FCSTD DOCUMENT  (FreeCAD 0.19R24276 (Git))
Label: assembly_1
License: All rights reserved
LicenseURL: http://en.wikipedia.org/wiki/All_rights_reserved
objects: Part::FeaturePython×82, App::LinkGroup×14, App::FeaturePython×4
note: 82 computed .brp shape members not serialized (recipe doc carries the construction recipe); baked Part::Feature solids carry a one-line shape summary decoded from their .brp

FEATURE [Part::FeaturePython] b_motor_mount_001_  label="motor mount_001"  # a2plus imported part (geometry in sourceFile) (typed FeaturePython)
  Placement = pos=(149.38,107.654,7.41064) rot=(-0.700909,0.71325,0;3.14159rad)
  a2p_Version = V0.1
  fixedPosition = false
  objectType = a2pPart
  sourceFile = ./../standard_parts/motor mount.FCStd
  subassemblyImport = false
  timeLastImport = 1.63751e+09
  updateColors = true
FEATURE [Part::FeaturePython] b_motor_mount_001_001  label="motor mount_002"  # a2plus imported part (geometry in sourceFile) (typed FeaturePython)
  Placement = pos=(-148.997,67.9961,7.41064) rot=(0.707107,0.707107,0;3.14159rad)
  a2p_Version = V0.1
  fixedPosition = false
  objectType = a2pPart
  sourceFile = ./../standard_parts/motor mount.FCStd
  subassemblyImport = false
  timeLastImport = 1.63751e+09
  updateColors = true
FEATURE [Part::FeaturePython] b_wheel1_001_  label="wheel1_001"  # a2plus imported part (geometry in sourceFile) (typed FeaturePython)
  Placement = pos=(-170.202,87.0329,-30.5973) rot=(0,0,1;0rad)
  a2p_Version = V0.1
  fixedPosition = false
  objectType = a2pPart
  sourceFile = ./../ROS_Bot_1/my 3D/ASSEM/wheel.stp
  subassemblyImport = false
  timeLastImport = 1.63742e+09
  updateColors = true
FEATURE [Part::FeaturePython] b_motor1_001_  label="motor1_001"  # a2plus imported part (geometry in sourceFile) (typed FeaturePython)
  Placement = pos=(133.059,87.9604,-23.6086) rot=(0.999922,-0.008726,-0.00888;1.55342rad)
  a2p_Version = V0.1
  fixedPosition = false
  objectType = a2pPart
  sourceFile = ./../ROS_Bot_1/my 3D/ASSEM/motor.stp
  subassemblyImport = false
  timeLastImport = 1.6374e+09
  updateColors = true
FEATURE [App::FeaturePython] axisCoincident_003  label="axisCoincident_003__motor1_001"  # a2plus constraint (typed FeaturePython)
  Object1 = b_motor_mount_001_
  Object2 = b_motor1_001_
  ParentTreeObject = -> b_motor_mount_001_
  SubElement1 = Face28
  SubElement2 = Face12
  Suppressed = false
  Type = axial
  directionConstraint = 1
  lockRotation = false
FEATURE [App::FeaturePython] axisCoincident_003_mirror  label="axisCoincident_003__motor mount_001"  # a2plus constraint (typed FeaturePython)
  Object1 = b_motor_mount_001_
  Object2 = b_motor1_001_
  ParentTreeObject = -> b_motor1_001_
  SubElement1 = Face28
  SubElement2 = Face12
  Suppressed = false
  Type = axial
  directionConstraint = 1
  lockRotation = false
FEATURE [App::FeaturePython] axisCoincident_004  label="axisCoincident_004__motor mount_001"  # a2plus constraint (typed FeaturePython)
  Object1 = b_motor1_001_
  Object2 = b_motor_mount_001_
  ParentTreeObject = -> b_motor1_001_
  SubElement1 = Face12
  SubElement2 = Face28
  Suppressed = false
  Type = axial
  directionConstraint = 0
  lockRotation = true
FEATURE [App::FeaturePython] axisCoincident_004_mirror  label="axisCoincident_004__motor1_001"  # a2plus constraint (typed FeaturePython)
  Object1 = b_motor1_001_
  Object2 = b_motor_mount_001_
  ParentTreeObject = -> b_motor_mount_001_
  SubElement1 = Face12
  SubElement2 = Face28
  Suppressed = false
  Type = axial
  directionConstraint = 0
  lockRotation = true
FEATURE [Part::FeaturePython] b_motor1_001_001  label="motor1_002"  # a2plus imported part (geometry in sourceFile) (typed FeaturePython)
  Placement = pos=(-133.004,87.4074,-23.2076) rot=(0.00011,0.700908,0.713251;3.1418rad)
  a2p_Version = V0.1
  fixedPosition = false
  objectType = a2pPart
  sourceFile = ./../ROS_Bot_1/my 3D/ASSEM/motor.stp
  subassemblyImport = false
  timeLastImport = 1.6374e+09
  updateColors = true
FEATURE [Part::FeaturePython] b_wheel1_001_001  label="wheel1_002"  # a2plus imported part (geometry in sourceFile) (typed FeaturePython)
  Placement = pos=(160.198,87.0329,-30.5973) rot=(0,0,1;0rad)
  a2p_Version = V0.1
  fixedPosition = false
  objectType = a2pPart
  sourceFile = ./../ROS_Bot_1/my 3D/ASSEM/wheel.stp
  subassemblyImport = false
  timeLastImport = 1.63742e+09
  updateColors = true
FEATURE [Part::FeaturePython] b_motor_driver_board_001_  label="motor driver board_001"  # a2plus imported part (geometry in sourceFile) (typed FeaturePython)
  Placement = pos=(-45.0132,88.1039,15.6672) rot=(0,0,-1;1.5708rad)
  a2p_Version = V0.1
  fixedPosition = false
  objectType = a2pPart
  sourceFile = ./../standard_parts/motor driver/motor driver board.FCStd
  subassemblyImport = false
  timeLastImport = 1.63729e+09
  updateColors = true
FEATURE [Part::FeaturePython] b_base_1_001_  label="base_1_001"  # a2plus imported part (geometry in sourceFile) (typed FeaturePython)
  a2p_Version = V0.1
  fixedPosition = true
  objectType = a2pPart
  sourceFile = ./base_1.FCStd
  subassemblyImport = false
  timeLastImport = 1.65701e+09
  updateColors = true
FEATURE [Part::FeaturePython] b_top_001_  label="top_001"  # a2plus imported part (geometry in sourceFile) (typed FeaturePython)
  Placement = pos=(-0.376892,0.553345,71.2288) rot=(0,0,1;0rad)
  a2p_Version = V0.1
  fixedPosition = false
  objectType = a2pPart
  sourceFile = ./top.FCStd
  subassemblyImport = false
  timeLastImport = 1.65701e+09
  updateColors = true
FEATURE [Part::FeaturePython] b_lidar1_001_  label="lidar1_001"  # a2plus imported part (geometry in sourceFile) (typed FeaturePython)
  Placement = pos=(36.9558,-4.98086,81.9191) rot=(0.57735,-0.57735,-0.57735;2.0944rad)
  a2p_Version = V0.1
  fixedPosition = false
  objectType = a2pPart
  sourceFile = ./../standard_parts/lidar.stp
  subassemblyImport = false
  timeLastImport = 1.6374e+09
  updateColors = true
FEATURE [Part::FeaturePython] b_guide_wheel1_001_  label="guide_wheel1_001"  # a2plus imported part (geometry in sourceFile) (typed FeaturePython)
  Placement = pos=(-9.92305,-140.014,-21.8192) rot=(0,0,-1;0.017453rad)
  a2p_Version = V0.1
  fixedPosition = false
  objectType = a2pPart
  sourceFile = ./guide_wheel.step
  subassemblyImport = false
  timeLastImport = 1.65702e+09
  updateColors = true
FEATURE [Part::FeaturePython] b_RPi1_001_  label="RPi1_001"  # a2plus imported part (geometry in sourceFile) (typed FeaturePython)
  Placement = pos=(29.8566,29.4806,88.8306) rot=(0.57735,0.57735,0.57735;2.0944rad)
  a2p_Version = V0.1
  fixedPosition = false
  objectType = a2pPart
  sourceFile = ./RPi.step
  subassemblyImport = false
  timeLastImport = 1.65702e+09
  updateColors = true
FEATURE [Part::FeaturePython] b_Atd1_001_  label="Atd1_001"  # a2plus imported part (geometry in sourceFile) (typed FeaturePython)
  Placement = pos=(0.456543,-67.9815,20.7461) rot=(0.707107,-0.707107,0;3.14159rad)
  a2p_Version = V0.1
  fixedPosition = false
  objectType = a2pPart
  sourceFile = ./Atd.step
  subassemblyImport = false
  timeLastImport = 1.65702e+09
  updateColors = true
FEATURE [Part::FeaturePython] b_stand1_001_  label="stand1_001"  # a2plus imported part (geometry in sourceFile) (typed FeaturePython)
  Placement = pos=(-10.3015,-141.085,4.0706) rot=(0,0,1;0rad)
  a2p_Version = V0.1
  fixedPosition = false
  objectType = a2pPart
  sourceFile = ./stand.step
  subassemblyImport = false
  timeLastImport = 1.65702e+09
  updateColors = true
FEATURE [Part::FeaturePython] PcbSpacer  label="M5x8x10-Spacer"  # WARN: FeaturePython — macro-defined, semantics opaque (R4)
  Placement = pos=(24.1,-22.24,10) rot=(0,0,1;0rad)
  baseObject = -> b_base_1_001_ [Edge135]
  diameter = 4
  invert = false
  length = 0
  offset = 0
  width = 0
FEATURE [Part::FeaturePython] PcbSpacer002  label="M5x8x10-Spacer002"  # WARN: FeaturePython — macro-defined, semantics opaque (R4)
  Placement = pos=(-25.12,-29.42,10) rot=(0,0,1;0rad)
  baseObject = -> b_base_1_001_ [Edge125]
  diameter = 4
  invert = false
  length = 0
  offset = 0
  width = 0
FEATURE [Part::FeaturePython] PcbSpacer004  label="M5x8x10-Spacer004"  # WARN: FeaturePython — macro-defined, semantics opaque (R4)
  Placement = pos=(-24.52,-104.82,10) rot=(0,0,1;0rad)
  baseObject = -> b_base_1_001_ [Edge123]
  diameter = 4
  invert = false
  length = 0
  offset = 0
  width = 0
FEATURE [Part::FeaturePython] PcbSpacer006  label="M5x8x10-Spacer006"  # WARN: FeaturePython — macro-defined, semantics opaque (R4)
  Placement = pos=(24.1,-104.82,10) rot=(0,0,1;0rad)
  baseObject = -> b_base_1_001_ [Edge131]
  diameter = 4
  invert = false
  length = 0
  offset = 0
  width = 0
FEATURE [App::LinkGroup] LinkGroup
  ElementList = -> [PcbSpacer,PcbSpacer002,PcbSpacer004,PcbSpacer006]
  LinkMode = 0
  Placement = pos=(0,-3.8147e-06,-3.8147e-06) rot=(0,0,1;0rad)
FEATURE [Part::FeaturePython] PcbSpacer007  label="M4x7x5-Spacer"  # WARN: FeaturePython — macro-defined, semantics opaque (R4)
  Placement = pos=(34.12,85.08,10) rot=(0,0,1;0rad)
  baseObject = -> b_base_1_001_ [Edge173]
  diameter = 3
  invert = false
  length = 0
  offset = 0
  width = 0
FEATURE [Part::FeaturePython] PcbSpacer009  label="M4x7x5-Spacer002"  # WARN: FeaturePython — macro-defined, semantics opaque (R4)
  Placement = pos=(-21.75,85.08,10) rot=(0,0,1;0rad)
  baseObject = -> b_base_1_001_ [Edge157]
  diameter = 3
  invert = false
  length = 0
  offset = 0
  width = 0
FEATURE [Part::FeaturePython] PcbSpacer011  label="M4x7x5-Spacer004"  # WARN: FeaturePython — macro-defined, semantics opaque (R4)
  Placement = pos=(34.12,6.36,10) rot=(0,0,1;0rad)
  baseObject = -> b_base_1_001_ [Edge171]
  diameter = 3
  invert = false
  length = 0
  offset = 0
  width = 0
FEATURE [Part::FeaturePython] PcbSpacer013  label="M4x7x5-Spacer006"  # WARN: FeaturePython — macro-defined, semantics opaque (R4)
  Placement = pos=(-21.75,6.36,10) rot=(0,0,1;0rad)
  baseObject = -> b_base_1_001_ [Edge155]
  diameter = 3
  invert = false
  length = 0
  offset = 0
  width = 0
FEATURE [App::LinkGroup] LinkGroup001
  ElementList = -> [PcbSpacer007,PcbSpacer009,PcbSpacer011,PcbSpacer013]
  LinkMode = 0
  Placement = pos=(0,2.38419e-07,-9.53674e-07) rot=(0,0,1;0rad)
FEATURE [Part::FeaturePython] Screw001  label="M2.5x3-Screw"  # Fasteners workbench fastener (typed FeaturePython)
  Placement = pos=(-25.6369,-11.9567,71.2288) rot=(-1,0,0;3.14159rad)
  baseObject = -> b_top_001_ [Edge32]
  diameter = 3
  invert = true
  length = 0
  lengthCustom = 3
  matchOuter = false
  offset = 0
  thread = false
  type = 35
FEATURE [Part::FeaturePython] Screw003  label="M2.5x3-Screw015"  # Fasteners workbench fastener (typed FeaturePython)
  Placement = pos=(30.3331,-11.9567,71.2288) rot=(-1,0,0;3.14159rad)
  baseObject = -> b_top_001_ [Edge36]
  diameter = 3
  invert = true
  length = 0
  lengthCustom = 3
  matchOuter = false
  offset = 0
  thread = false
  type = 35
FEATURE [Part::FeaturePython] Screw005  label="M2.5x3-Screw016"  # Fasteners workbench fastener (typed FeaturePython)
  Placement = pos=(-18.1469,-81.9067,71.2288) rot=(-1,0,0;3.14159rad)
  baseObject = -> b_top_001_ [Edge28]
  diameter = 3
  invert = true
  length = 0
  lengthCustom = 3
  matchOuter = false
  offset = 0
  thread = false
  type = 35
FEATURE [Part::FeaturePython] Screw007  label="M2.5x3-Screw017"  # Fasteners workbench fastener (typed FeaturePython)
  Placement = pos=(22.8531,-81.9667,71.2288) rot=(-1,0,0;3.14159rad)
  baseObject = -> b_top_001_ [Edge30]
  diameter = 3
  invert = true
  length = 0
  lengthCustom = 3
  matchOuter = false
  offset = 0
  thread = false
  type = 35
FEATURE [App::LinkGroup] LinkGroup002
  ElementList = -> [Screw001,Screw003,Screw005,Screw007]
  LinkMode = 0
FEATURE [Part::FeaturePython] Screw  label="M4x5-Screw"  # Fasteners workbench fastener (typed FeaturePython)
  Placement = pos=(-148.997,103.616,-23.3051) rot=(0,-1,0;1.5708rad)
  baseObject = -> b_motor_mount_001_001 [Edge55]
  diameter = 6
  invert = true
  length = 0
  lengthCustom = 5
  matchOuter = false
  offset = 0
  thread = false
  type = 35
FEATURE [Part::FeaturePython] Screw009  label="M4x5-Screw001"  # Fasteners workbench fastener (typed FeaturePython)
  Placement = pos=(-150.497,72.6161,-23.3051) rot=(0,-1,0;1.5708rad)
  baseObject = -> b_motor_mount_001_001 [Edge47]
  diameter = 3
  invert = true
  length = 0
  lengthCustom = 5
  matchOuter = false
  offset = 0
  thread = false
  type = 15
FEATURE [App::LinkGroup] LinkGroup003
  ElementList = -> [Screw,Screw009]
  LinkMode = 0
FEATURE [Part::FeaturePython] Screw010  label="(M3.5)x5-Screw"  # Fasteners workbench fastener (typed FeaturePython)
  Placement = pos=(-18.9165,-178.267,10) rot=(0,0,1;0rad)
  baseObject = -> b_base_1_001_ [Edge121]
  diameter = 5
  invert = false
  length = 0
  lengthCustom = 5
  matchOuter = false
  offset = 0
  thread = false
  type = 35
FEATURE [Part::FeaturePython] Screw012  label="(M3.5)x5-Screw002"  # Fasteners workbench fastener (typed FeaturePython)
  Placement = pos=(11.0877,-179.124,10) rot=(0,0,1;0rad)
  baseObject = -> b_base_1_001_ [Edge129]
  diameter = 5
  invert = false
  length = 0
  lengthCustom = 5
  matchOuter = false
  offset = 0
  thread = false
  type = 35
FEATURE [Part::FeaturePython] Screw014  label="(M3.5)x5-Screw004"  # Fasteners workbench fastener (typed FeaturePython)
  Placement = pos=(10.4284,-203.085,10) rot=(0,0,1;0rad)
  baseObject = -> b_base_1_001_ [Edge127]
  diameter = 5
  invert = false
  length = 0
  lengthCustom = 5
  matchOuter = false
  offset = 0
  thread = false
  type = 35
FEATURE [Part::FeaturePython] Screw016  label="(M3.5)x5-Screw006"  # Fasteners workbench fastener (typed FeaturePython)
  Placement = pos=(-19.5947,-202.247,10) rot=(0,0,1;0rad)
  baseObject = -> b_base_1_001_ [Edge119]
  diameter = 5
  invert = false
  length = 0
  lengthCustom = 5
  matchOuter = false
  offset = 0
  thread = false
  type = 35
FEATURE [App::LinkGroup] LinkGroup004
  ElementList = -> [Screw010,Screw012,Screw014,Screw016]
  LinkMode = 0
FEATURE [Part::FeaturePython] Screw017  label="M4x5-Screw006"  # Fasteners workbench fastener (typed FeaturePython)
  Placement = pos=(148.758,72.0392,-23.3051) rot=(0.017452,0.999848,0;1.5708rad)
  baseObject = -> b_motor_mount_001_ [Edge55]
  diameter = 6
  invert = true
  length = 0
  lengthCustom = 5
  matchOuter = false
  offset = 0
  thread = false
  type = 35
FEATURE [Part::FeaturePython] Screw020  label="M4x5-Screw007"  # Fasteners workbench fastener (typed FeaturePython)
  Placement = pos=(150.799,103.008,-23.3051) rot=(0.017452,0.999848,0;1.5708rad)
  baseObject = -> b_motor_mount_001_ [Edge47]
  diameter = 6
  invert = true
  length = 0
  lengthCustom = 5
  matchOuter = false
  offset = 0
  thread = false
  type = 35
FEATURE [App::LinkGroup] LinkGroup005
  ElementList = -> [Screw017,Screw020]
  LinkMode = 0
FEATURE [Part::FeaturePython] b_fastener_motor_mount1_001_  label="fastener_motor_mount1_001"  # a2plus imported part (geometry in sourceFile) (typed FeaturePython)
  Placement = pos=(42.7042,-41.7847,3.72639) rot=(0,0,1;0rad)
  a2p_Version = V0.1
  fixedPosition = false
  objectType = a2pPart
  sourceFile = ./fastener_motor_mount.step
  subassemblyImport = false
  timeLastImport = 1.65702e+09
  updateColors = true
FEATURE [Part::FeaturePython] b_fastener_motor_mount1_001_001  label="fastener_motor_mount1_002"  # a2plus imported part (geometry in sourceFile) (typed FeaturePython)
  Placement = pos=(-212.296,-41.7847,3.72639) rot=(0,0,1;0rad)
  a2p_Version = V0.1
  fixedPosition = false
  objectType = a2pPart
  sourceFile = ./fastener_motor_mount.step
  subassemblyImport = false
  timeLastImport = 1.65702e+09
  updateColors = true
FEATURE [Part::FeaturePython] PcbSpacer014  label="M4x7x5-Spacer007"  # WARN: FeaturePython — macro-defined, semantics opaque (R4)
  Placement = pos=(26.1131,91.2133,81.2288) rot=(0,0,1;0rad)
  baseObject = -> b_top_001_ [Edge117]
  diameter = 3
  invert = false
  length = 0
  offset = 0
  width = 0
FEATURE [Part::FeaturePython] PcbSpacer016  label="M4x7x5-Spacer009"  # WARN: FeaturePython — macro-defined, semantics opaque (R4)
  Placement = pos=(-22.8769,91.2633,81.2288) rot=(0,0,1;0rad)
  baseObject = -> b_top_001_ [Edge109]
  diameter = 3
  invert = false
  length = 0
  offset = 0
  width = 0
FEATURE [Part::FeaturePython] PcbSpacer018  label="M4x7x5-Spacer011"  # WARN: FeaturePython — macro-defined, semantics opaque (R4)
  Placement = pos=(26.1131,33.2133,81.2288) rot=(0,0,1;0rad)
  baseObject = -> b_top_001_ [Edge113]
  diameter = 3
  invert = false
  length = 0
  offset = 0
  width = 0
FEATURE [Part::FeaturePython] PcbSpacer020  label="M4x7x5-Spacer013"  # WARN: FeaturePython — macro-defined, semantics opaque (R4)
  Placement = pos=(-22.8969,33.2133,81.2288) rot=(0,0,1;0rad)
  baseObject = -> b_top_001_ [Edge105]
  diameter = 3
  invert = false
  length = 0
  offset = 0
  width = 0
FEATURE [App::LinkGroup] LinkGroup006
  ElementList = -> [PcbSpacer014,PcbSpacer016,PcbSpacer018,PcbSpacer020]
  LinkMode = 0
  Placement = pos=(0,-1.90735e-06,0.999985) rot=(0,0,1;0rad)
FEATURE [Part::FeaturePython] Screw022  label="M4x5-Screw016"  # Fasteners workbench fastener (typed FeaturePython)
  Placement = pos=(24.1,-22.24,0) rot=(-1,0,0;3.14159rad)
  baseObject = -> b_base_1_001_ [Edge34]
  diameter = 6
  invert = true
  length = 0
  lengthCustom = 5
  matchOuter = false
  offset = 0
  thread = false
  type = 35
FEATURE [Part::FeaturePython] Screw024  label="M4x5-Screw017"  # Fasteners workbench fastener (typed FeaturePython)
  Placement = pos=(24.1,-104.82,0) rot=(-1,0,0;3.14159rad)
  baseObject = -> b_base_1_001_ [Edge32]
  diameter = 6
  invert = true
  length = 0
  lengthCustom = 5
  matchOuter = false
  offset = 0
  thread = false
  type = 35
FEATURE [Part::FeaturePython] Screw026  label="M4x5-Screw018"  # Fasteners workbench fastener (typed FeaturePython)
  Placement = pos=(-25.12,-29.42,0) rot=(-1,0,0;3.14159rad)
  baseObject = -> b_base_1_001_ [Edge29]
  diameter = 6
  invert = true
  length = 0
  lengthCustom = 5
  matchOuter = false
  offset = 0
  thread = false
  type = 35
FEATURE [Part::FeaturePython] Screw028  label="M4x5-Screw019"  # Fasteners workbench fastener (typed FeaturePython)
  Placement = pos=(-24.52,-104.82,0) rot=(-1,0,0;3.14159rad)
  baseObject = -> b_base_1_001_ [Edge28]
  diameter = 6
  invert = true
  length = 0
  lengthCustom = 5
  matchOuter = false
  offset = 0
  thread = false
  type = 35
FEATURE [App::LinkGroup] LinkGroup007
  ElementList = -> [Screw022,Screw024,Screw026,Screw028]
  LinkMode = 0
FEATURE [Part::FeaturePython] Screw030  label="(M3.5)x5-Screw016"  # Fasteners workbench fastener (typed FeaturePython)
  Placement = pos=(34.12,6.36,0) rot=(-1,0,0;3.14159rad)
  baseObject = -> b_base_1_001_ [Edge52]
  diameter = 5
  invert = true
  length = 0
  lengthCustom = 5
  matchOuter = false
  offset = 0
  thread = false
  type = 35
FEATURE [Part::FeaturePython] Screw032  label="(M3.5)x5-Screw018"  # Fasteners workbench fastener (typed FeaturePython)
  Placement = pos=(34.12,85.08,0) rot=(-1,0,0;3.14159rad)
  baseObject = -> b_base_1_001_ [Edge53]
  diameter = 5
  invert = true
  length = 0
  lengthCustom = 5
  matchOuter = false
  offset = 0
  thread = false
  type = 35
FEATURE [Part::FeaturePython] Screw034  label="(M3.5)x5-Screw020"  # Fasteners workbench fastener (typed FeaturePython)
  Placement = pos=(-21.75,6.36,0) rot=(-1,0,0;3.14159rad)
  baseObject = -> b_base_1_001_ [Edge44]
  diameter = 5
  invert = true
  length = 0
  lengthCustom = 5
  matchOuter = false
  offset = 0
  thread = false
  type = 35
FEATURE [Part::FeaturePython] Screw036  label="(M3.5)x5-Screw022"  # Fasteners workbench fastener (typed FeaturePython)
  Placement = pos=(-21.75,85.08,0) rot=(-1,0,0;3.14159rad)
  baseObject = -> b_base_1_001_ [Edge45]
  diameter = 5
  invert = true
  length = 0
  lengthCustom = 5
  matchOuter = false
  offset = 0
  thread = false
  type = 35
FEATURE [App::LinkGroup] LinkGroup008
  ElementList = -> [Screw030,Screw032,Screw034,Screw036]
  LinkMode = 0
FEATURE [Part::FeaturePython] Screw045  label="(M3.5)x5-Screw041"  # Fasteners workbench fastener (typed FeaturePython)
  Placement = pos=(26.3566,90.9806,88.8306) rot=(0,0,1;0rad)
  baseObject = -> b_RPi1_001_ [Edge543]
  diameter = 5
  invert = false
  length = 0
  lengthCustom = 5
  matchOuter = false
  offset = 0
  thread = false
  type = 35
FEATURE [Part::FeaturePython] Screw047  label="(M3.5)x5-Screw042"  # Fasteners workbench fastener (typed FeaturePython)
  Placement = pos=(-22.6434,90.9806,88.8306) rot=(0,0,1;0rad)
  baseObject = -> b_RPi1_001_ [Edge554]
  diameter = 5
  invert = false
  length = 0
  lengthCustom = 5
  matchOuter = false
  offset = 0
  thread = false
  type = 35
FEATURE [Part::FeaturePython] Screw050  label="(M3.5)x5-Screw043"  # Fasteners workbench fastener (typed FeaturePython)
  Placement = pos=(-22.6434,32.9806,90.3038) rot=(0,0,1;0rad)
  baseObject = -> b_RPi1_001_ [Edge519]
  diameter = 5
  invert = false
  length = 0
  lengthCustom = 5
  matchOuter = false
  offset = 0
  thread = false
  type = 35
FEATURE [Part::FeaturePython] Screw052  label="(M3.5)x5-Screw044"  # Fasteners workbench fastener (typed FeaturePython)
  Placement = pos=(26.3566,32.9806,90.3038) rot=(0,0,1;0rad)
  baseObject = -> b_RPi1_001_ [Edge521]
  diameter = 5
  invert = false
  length = 0
  lengthCustom = 5
  matchOuter = false
  offset = 0
  thread = false
  type = 35
FEATURE [App::LinkGroup] LinkGroup009
  ElementList = -> [Screw045,Screw047,Screw050,Screw052]
  LinkMode = 0
FEATURE [Part::FeaturePython] b_base_1_001_001  label="base_1_002"  # a2plus imported part (geometry in sourceFile) (typed FeaturePython)
  a2p_Version = V0.1
  fixedPosition = true
  objectType = a2pPart
  sourceFile = ./base_1.FCStd
  subassemblyImport = false
  timeLastImport = 1.65701e+09
  updateColors = true
FEATURE [Part::FeaturePython] PcbSpacer022  label="M6x10x60-Spacer004"  # WARN: FeaturePython — macro-defined, semantics opaque (R4)
  Placement = pos=(125,-168,9) rot=(0,0,1;0rad)
  diameter = 5
  invert = false
  length = 9
  offset = 0
  width = 0
FEATURE [Part::FeaturePython] PcbSpacer023  label="M6x10x60-Spacer"  # WARN: FeaturePython — macro-defined, semantics opaque (R4)
  Placement = pos=(125,135,11) rot=(0,0,1;0rad)
  diameter = 5
  invert = false
  length = 9
  offset = 0
  width = 0
FEATURE [Part::FeaturePython] PcbSpacer024  label="M6x10x60-Spacer001"  # WARN: FeaturePython — macro-defined, semantics opaque (R4)
  Placement = pos=(-123,136,9) rot=(0,0,1;0rad)
  diameter = 5
  invert = false
  length = 9
  offset = 0
  width = 0
FEATURE [Part::FeaturePython] PcbSpacer025  label="M6x10x60-Spacer002"  # WARN: FeaturePython — macro-defined, semantics opaque (R4)
  Placement = pos=(-125,32,10) rot=(0,0,1;0rad)
  baseObject = -> b_base_1_001_ [Edge137]
  diameter = 5
  invert = false
  length = 9
  offset = 0
  width = 0
FEATURE [Part::FeaturePython] PcbSpacer027  label="M6x10x60-Spacer003"  # WARN: FeaturePython — macro-defined, semantics opaque (R4)
  Placement = pos=(-125,-168,10) rot=(0,0,1;0rad)
  baseObject = -> b_base_1_001_ [Edge117]
  diameter = 5
  invert = false
  length = 9
  offset = 0
  width = 0
FEATURE [App::LinkGroup] LinkGroup011
  ElementList = -> [PcbSpacer024,PcbSpacer025,PcbSpacer027]
  LinkMode = 0
FEATURE [Part::FeaturePython] PcbSpacer028  label="M6x10x60-Spacer005"  # WARN: FeaturePython — macro-defined, semantics opaque (R4)
  Placement = pos=(125,32,11) rot=(0,0,1;0rad)
  diameter = 5
  invert = false
  length = 9
  offset = 0
  width = 0
FEATURE [App::LinkGroup] LinkGroup010
  ElementList = -> [PcbSpacer023,PcbSpacer022,PcbSpacer028]
  LinkMode = 0
FEATURE [Part::FeaturePython] Screw054  label="M10x12-Screw"  # Fasteners workbench fastener (typed FeaturePython)
  Placement = pos=(-125,32,0) rot=(-1,0,0;3.14159rad)
  baseObject = -> b_base_1_001_ [Edge35]
  diameter = 10
  invert = true
  length = 0
  lengthCustom = 12
  matchOuter = false
  offset = 0
  thread = false
  type = 35
FEATURE [Part::FeaturePython] Screw056  label="M10x12-Screw001"  # Fasteners workbench fastener (typed FeaturePython)
  Placement = pos=(125,32,0) rot=(-1,0,0;3.14159rad)
  baseObject = -> b_base_1_001_ [Edge54]
  diameter = 10
  invert = true
  length = 0
  lengthCustom = 12
  matchOuter = false
  offset = 0
  thread = false
  type = 35
FEATURE [Part::FeaturePython] Screw058  label="M10x12-Screw006"  # Fasteners workbench fastener (typed FeaturePython)
  Placement = pos=(-125,137,0) rot=(-1,0,0;3.14159rad)
  baseObject = -> b_base_1_001_ [Edge50]
  diameter = 10
  invert = true
  length = 0
  lengthCustom = 12
  matchOuter = false
  offset = 0
  thread = false
  type = 35
FEATURE [Part::FeaturePython] Screw060  label="M10x12-Screw007"  # Fasteners workbench fastener (typed FeaturePython)
  Placement = pos=(125,137,0) rot=(-1,0,0;3.14159rad)
  baseObject = -> b_base_1_001_ [Edge67]
  diameter = 10
  invert = true
  length = 0
  lengthCustom = 12
  matchOuter = false
  offset = 0
  thread = false
  type = 35
FEATURE [Part::FeaturePython] Screw062  label="M10x12-Screw012"  # Fasteners workbench fastener (typed FeaturePython)
  Placement = pos=(-125,-168,0) rot=(-1,0,0;3.14159rad)
  baseObject = -> b_base_1_001_ [Edge25]
  diameter = 10
  invert = true
  length = 0
  lengthCustom = 12
  matchOuter = false
  offset = 0
  thread = false
  type = 35
FEATURE [Part::FeaturePython] Screw064  label="M10x12-Screw011"  # Fasteners workbench fastener (typed FeaturePython)
  Placement = pos=(125,-168,0) rot=(-1,0,0;3.14159rad)
  baseObject = -> b_base_1_001_ [Edge33]
  diameter = 10
  invert = true
  length = 0
  lengthCustom = 12
  matchOuter = false
  offset = 0
  thread = false
  type = 35
FEATURE [App::LinkGroup] LinkGroup012
  ElementList = -> [Screw064,Screw054,Screw056,Screw058,Screw060,Screw062]
  LinkMode = 0
FEATURE [Part::FeaturePython] Screw065  label="M10x12-Screw013"  # Fasteners workbench fastener (typed FeaturePython)
  Placement = pos=(-125.387,137.553,81.2288) rot=(0,0,1;0rad)
  baseObject = -> b_top_001_ [Edge107]
  diameter = 10
  invert = false
  length = 0
  lengthCustom = 12
  matchOuter = false
  offset = 0
  thread = false
  type = 35
FEATURE [Part::FeaturePython] Screw067  label="M10x12-Screw015"  # Fasteners workbench fastener (typed FeaturePython)
  Placement = pos=(-125.387,32.7033,81.2288) rot=(0,0,1;0rad)
  baseObject = -> b_top_001_ [Edge101]
  diameter = 10
  invert = false
  length = 0
  lengthCustom = 12
  matchOuter = false
  offset = 0
  thread = false
  type = 35
FEATURE [Part::FeaturePython] Screw069  label="M10x12-Screw017"  # Fasteners workbench fastener (typed FeaturePython)
  Placement = pos=(-125.387,-167.457,81.2288) rot=(0,0,1;0rad)
  baseObject = -> b_top_001_ [Edge85]
  diameter = 10
  invert = false
  length = 0
  lengthCustom = 12
  matchOuter = false
  offset = 0
  thread = false
  type = 35
FEATURE [Part::FeaturePython] Screw071  label="M10x12-Screw019"  # Fasteners workbench fastener (typed FeaturePython)
  Placement = pos=(124.543,-167.457,81.2288) rot=(0,0,1;0rad)
  baseObject = -> b_top_001_ [Edge97]
  diameter = 10
  invert = false
  length = 0
  lengthCustom = 12
  matchOuter = false
  offset = 0
  thread = false
  type = 35
FEATURE [Part::FeaturePython] Screw073  label="M10x12-Screw021"  # Fasteners workbench fastener (typed FeaturePython)
  Placement = pos=(124.543,32.5333,81.2288) rot=(0,0,1;0rad)
  baseObject = -> b_top_001_ [Edge115]
  diameter = 10
  invert = false
  length = 0
  lengthCustom = 12
  matchOuter = false
  offset = 0
  thread = false
  type = 35
FEATURE [Part::FeaturePython] Screw075  label="M10x12-Screw023"  # Fasteners workbench fastener (typed FeaturePython)
  Placement = pos=(124.543,137.613,81.2288) rot=(0,0,1;0rad)
  baseObject = -> b_top_001_ [Edge119]
  diameter = 10
  invert = false
  length = 0
  lengthCustom = 12
  matchOuter = false
  offset = 0
  thread = false
  type = 35
FEATURE [App::LinkGroup] LinkGroup013
  ElementList = -> [Screw065,Screw067,Screw069,Screw071,Screw073,Screw075]
  LinkMode = 0
FEATURE [Part::FeaturePython] Nut  label="5/16in-Nut"  # Fasteners workbench fastener (typed FeaturePython)
  Placement = pos=(-19.3015,-204.085,-45.2294) rot=(0,0,1;0rad)
  baseObject = -> b_stand1_001_ [Edge67]
  diameter = 12
  invert = false
  matchOuter = false
  offset = 0
  thread = false
  type = 0
FEATURE [Part::FeaturePython] Nut001  label="5/16in-Nut001"  # Fasteners workbench fastener (typed FeaturePython)
  Placement = pos=(-19.3015,-204.085,-36.8294) rot=(0,0,1;0rad)
  baseObject = -> b_stand1_001_ [Edge65]
  diameter = 12
  invert = false
  matchOuter = false
  offset = 0
  thread = false
  type = 0
FEATURE [Part::FeaturePython] Nut002  label="5/16in-Nut002"  # Fasteners workbench fastener (typed FeaturePython)
  Placement = pos=(10.6985,-203.585,-45.0294) rot=(0,0,1;0rad)
  baseObject = -> b_stand1_001_ [Edge136]
  diameter = 2
  invert = false
  matchOuter = false
  offset = 0
  thread = false
  type = 1
FEATURE [Part::FeaturePython] Nut003  label="5/16in-Nut003"  # Fasteners workbench fastener (typed FeaturePython)
  Placement = pos=(10.6985,-203.585,-36.6294) rot=(0,0,1;0rad)
  baseObject = -> b_stand1_001_ [Edge134]
  diameter = 2
  invert = false
  matchOuter = false
  offset = 0
  thread = false
  type = 1
FEATURE [Part::FeaturePython] Nut004  label="5/16in-Nut004"  # Fasteners workbench fastener (typed FeaturePython)
  Placement = pos=(-19.8015,-180.085,-45.1294) rot=(0,0,1;0rad)
  baseObject = -> b_stand1_001_ [Edge274]
  diameter = 2
  invert = false
  matchOuter = false
  offset = 0
  thread = false
  type = 1
FEATURE [Part::FeaturePython] Nut005  label="5/16in-Nut005"  # Fasteners workbench fastener (typed FeaturePython)
  Placement = pos=(-19.8015,-180.085,-36.7294) rot=(0,0,1;0rad)
  baseObject = -> b_stand1_001_ [Edge272]
  diameter = 2
  invert = false
  matchOuter = false
  offset = 0
  thread = false
  type = 1
FEATURE [Part::FeaturePython] Nut006  label="5/16in-Nut006"  # Fasteners workbench fastener (typed FeaturePython)
  Placement = pos=(10.6985,-179.585,-45.0294) rot=(0,0,1;0rad)
  baseObject = -> b_stand1_001_ [Edge205]
  diameter = 2
  invert = false
  matchOuter = false
  offset = 0
  thread = false
  type = 1
FEATURE [Part::FeaturePython] Nut007  label="5/16in-Nut007"  # Fasteners workbench fastener (typed FeaturePython)
  Placement = pos=(10.6985,-179.585,-36.6294) rot=(0,0,1;0rad)
  baseObject = -> b_stand1_001_ [Edge203]
  diameter = 2
  invert = false
  matchOuter = false
  offset = 0
  thread = false
  type = 1
FEATURE [Part::FeaturePython] Screw077  label="(M3.5)x5-Screw049"  # Fasteners workbench fastener (typed FeaturePython)
  Placement = pos=(-22.8969,33.2133,71.2288) rot=(-1,0,0;3.14159rad)
  baseObject = -> b_top_001_ [Edge33]
  diameter = 5
  invert = true
  length = 0
  lengthCustom = 5
  matchOuter = false
  offset = 0
  thread = false
  type = 35
FEATURE [Part::FeaturePython] Screw079  label="(M3.5)x5-Screw050"  # Fasteners workbench fastener (typed FeaturePython)
  Placement = pos=(-22.8769,91.2633,71.2288) rot=(-1,0,0;3.14159rad)
  baseObject = -> b_top_001_ [Edge35]
  diameter = 5
  invert = true
  length = 0
  lengthCustom = 5
  matchOuter = false
  offset = 0
  thread = false
  type = 35
FEATURE [Part::FeaturePython] b_usb_camera_001_  label="usb camera_001"  # a2plus imported part (geometry in sourceFile) (typed FeaturePython)
  Placement = pos=(-52.0365,-238.642,71.5071) rot=(0,0,1;4.71239rad)
  a2p_Version = V0.1
  fixedPosition = false
  objectType = a2pPart
  sourceFile = ./usb camera.FCStd
  subassemblyImport = false
  timeLastImport = 1.65703e+09
  updateColors = true
